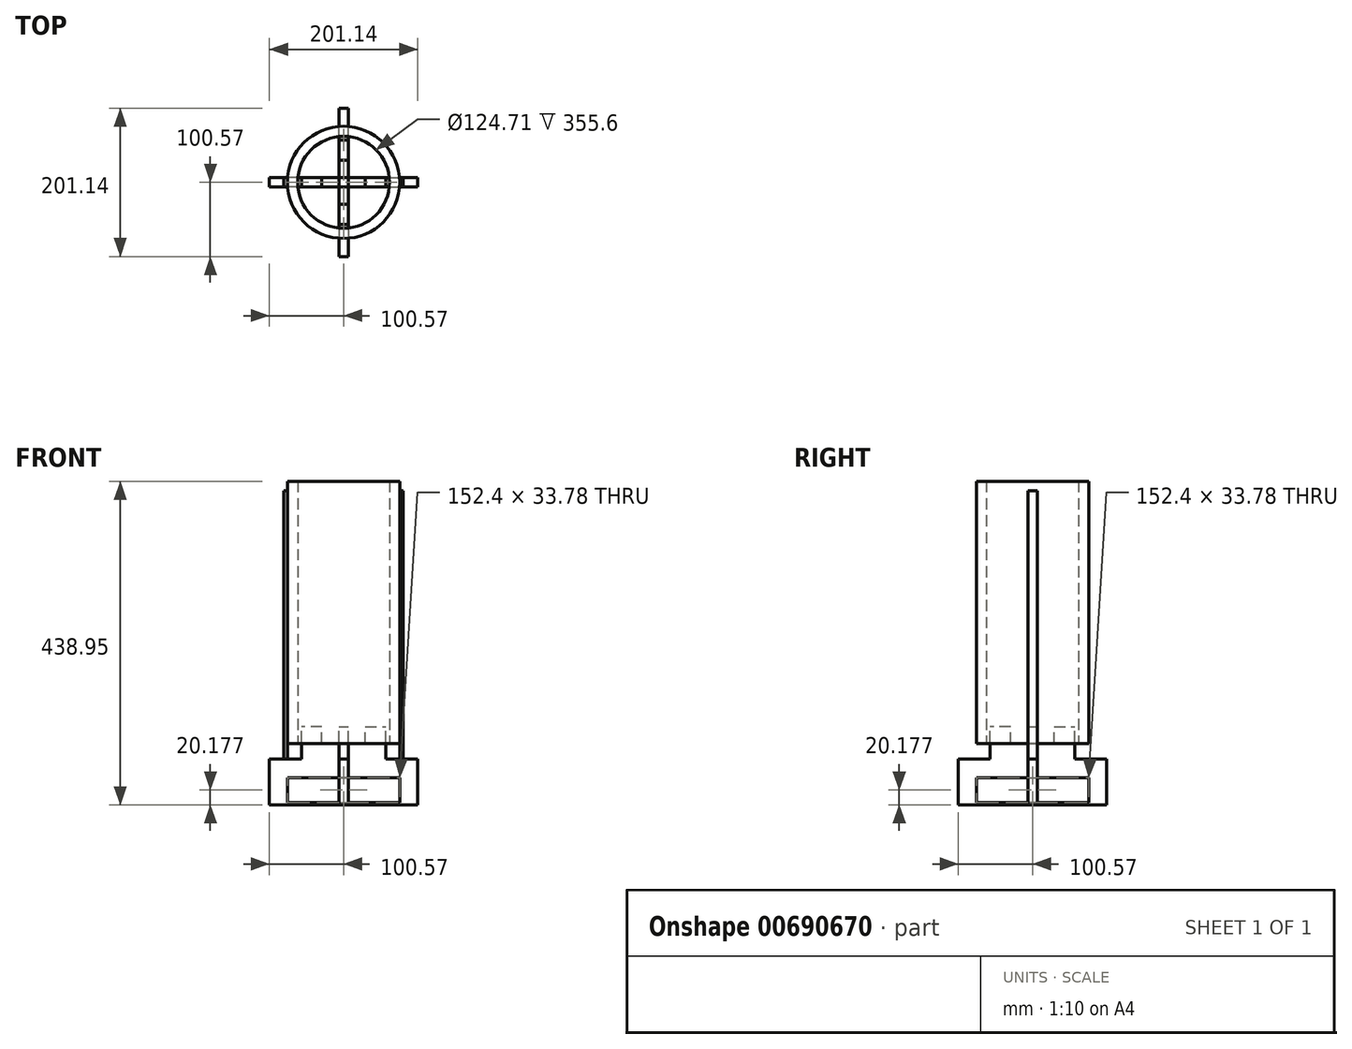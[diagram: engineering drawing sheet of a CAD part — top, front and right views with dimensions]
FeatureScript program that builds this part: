
annotation { "Feature Type Name" : "Feature", "Feature Type Description" : "" }
export const myFeature = defineFeature(function(context is Context, id is Id, definition is map)
    precondition{}
    {
        {
            var Q0;
            Q0=qCreatedBy(makeId("Top.planeOp"),FACE);
            var sketch = newSketch(context, id + "F0", { "sketchPlane" : qUnion([Q0])});
            skCircle(sketch, "E0", {"center": v(0, 0) * mm, "radius": 76.2 * mm});
            skCircle(sketch, "E1.0", {"center": v(0, 0) * mm, "radius": 62.36 * mm});
            skSolve(sketch);
        }
        {
            var Q0;
            Q0=qSketchRegion(id+"F0",true);
            extrude(context, id + "F1", {"entities" : qUnion([Q0]), "depth" : 355.6 * mm, "offsetDistance" : 25.4 * mm});
        }
        {
            var Q0;
            Q0=qCreatedBy(makeId("Front.planeOp"),FACE);
            var sketch = newSketch(context, id + "F2", { "sketchPlane" : qUnion([Q0])});
            skLineSegment(sketch, "E2", {"start": v(0, -20.88) * mm, "end": v(76.2, -20.88) * mm});
            skLineSegment(sketch, "E3", {"start": v(76.2, -46.28) * mm, "end": v(76.2, -25.4) * mm});
            skLineSegment(sketch, "E4", {"start": v(76.2, -46.28) * mm, "end": v(0, -46.28) * mm});
            skLineSegment(sketch, "E5", {"start": v(76.2, -20.88) * mm, "end": v(76.2, -46.28) * mm});
            skLineSegment(sketch, "E6", {"start": v(76.2, -46.28) * mm, "end": v(76.2, -46.28) * mm});
            skLineSegment(sketch, "E7", {"start": v(76.2, -25.4) * mm, "end": v(76.2, -46.28) * mm});
            skLineSegment(sketch, "E8", {"start": v(0, -20.88) * mm, "end": v(0, -46.28) * mm});
            skLineSegment(sketch, "E9.top", {"start": v(76.2, -83.35) * mm, "end": v(76.2, -83.35) * mm});
            skLineSegment(sketch, "E9.right", {"start": v(76.2, -25.4) * mm, "end": v(76.2, -83.35) * mm});
            skLineSegment(sketch, "E10.MirrorCS", {"start": v(-76.2, -46.28) * mm, "end": v(-76.2, -46.28) * mm});
            skLineSegment(sketch, "E11.MirrorCS", {"start": v(-76.2, -20.88) * mm, "end": v(-76.2, -46.28) * mm});
            skLineSegment(sketch, "E12.MirrorCS", {"start": v(-76.2, -25.4) * mm, "end": v(-76.2, -25.4) * mm});
            skLineSegment(sketch, "E13.MirrorCS", {"start": v(-76.2, -25.4) * mm, "end": v(-76.2, -83.35) * mm});
            skLineSegment(sketch, "E14.MirrorCS", {"start": v(-76.2, -46.28) * mm, "end": v(0, -46.28) * mm});
            skLineSegment(sketch, "E15.MirrorCS", {"start": v(-76.2, -46.28) * mm, "end": v(-76.2, -25.4) * mm});
            skLineSegment(sketch, "E16.MirrorCS", {"start": v(0, -20.88) * mm, "end": v(-76.2, -20.88) * mm});
            skLineSegment(sketch, "E17.MirrorCS", {"start": v(-76.2, -25.4) * mm, "end": v(-76.2, -46.28) * mm});
            skLineSegment(sketch, "E18.MirrorCS", {"start": v(-76.2, -83.35) * mm, "end": v(-76.2, -83.35) * mm});
            skLineSegment(sketch, "E19.bottom", {"start": v(-76.2, -83.35) * mm, "end": v(76.2, -83.35) * mm});
            skLineSegment(sketch, "E19.top", {"start": v(-76.2, -80.06) * mm, "end": v(76.2, -80.06) * mm});
            skLineSegment(sketch, "E19.left", {"start": v(-76.2, -83.35) * mm, "end": v(-76.2, -80.06) * mm});
            skLineSegment(sketch, "E19.right", {"start": v(76.2, -83.35) * mm, "end": v(76.2, -80.06) * mm});
            skLineSegment(sketch, "E20.bottom", {"start": v(76.2, -20.88) * mm, "end": v(100.57, -20.88) * mm});
            skLineSegment(sketch, "E20.top", {"start": v(76.2, -83.35) * mm, "end": v(100.57, -83.35) * mm});
            skLineSegment(sketch, "E20.left", {"start": v(76.2, -20.88) * mm, "end": v(76.2, -83.35) * mm});
            skLineSegment(sketch, "E20.right", {"start": v(100.57, -20.88) * mm, "end": v(100.57, -83.35) * mm});
            skLineSegment(sketch, "E21.MirrorCS", {"start": v(-100.57, -20.88) * mm, "end": v(-100.57, -83.35) * mm});
            skLineSegment(sketch, "E22.MirrorCS", {"start": v(-76.2, -20.88) * mm, "end": v(-100.57, -20.88) * mm});
            skLineSegment(sketch, "E23.MirrorCS", {"start": v(-76.2, -83.35) * mm, "end": v(-100.57, -83.35) * mm});
            skLineSegment(sketch, "E24.0", {"start": v(-62.36, 0) * mm, "end": v(62.36, 0) * mm});
            skLineSegment(sketch, "E25.bottom", {"start": v(0, -20.88) * mm, "end": v(57.23, -20.88) * mm});
            skLineSegment(sketch, "E25.top", {"start": v(0, 0) * mm, "end": v(57.23, 0) * mm});
            skLineSegment(sketch, "E25.left", {"start": v(0, -20.88) * mm, "end": v(0, 0) * mm});
            skLineSegment(sketch, "E25.right", {"start": v(57.23, -20.88) * mm, "end": v(57.23, 0) * mm});
            skLineSegment(sketch, "E26.bottom", {"start": v(29.62, 0) * mm, "end": v(57.23, 0) * mm});
            skLineSegment(sketch, "E26.top", {"start": v(29.62, 22.92) * mm, "end": v(57.23, 22.92) * mm});
            skLineSegment(sketch, "E26.left", {"start": v(29.62, 0) * mm, "end": v(29.62, 22.92) * mm});
            skLineSegment(sketch, "E26.right", {"start": v(57.23, 0) * mm, "end": v(57.23, 22.92) * mm});
            skLineSegment(sketch, "E27.MirrorCS", {"start": v(-29.62, 0) * mm, "end": v(-29.62, 22.92) * mm});
            skLineSegment(sketch, "E28.MirrorCS", {"start": v(-29.62, 22.92) * mm, "end": v(-57.23, 22.92) * mm});
            skLineSegment(sketch, "E29.MirrorCS", {"start": v(-57.23, 0) * mm, "end": v(-57.23, 22.92) * mm});
            skLineSegment(sketch, "E30.MirrorCS", {"start": v(-57.23, -20.88) * mm, "end": v(-57.23, 0) * mm});
            skSolve(sketch);
        }
        {
            var Q0;
            Q0=qSketchRegion(id+"F2",true);
            extrude(context, id + "F3", {"entities" : qUnion([Q0]), "endBound" : BoundingType.SYMMETRIC, "depth" : 12.7 * mm, "offsetDistance" : 25.4 * mm});
        }
        {
            var Q0;
            Q0=makeQuery(id+"F3.opExtrude","SWEPT_BODY",BODY,{"disambiguationData":[OSD([sQuery(id+"F2.wireOp",EDGE,"E2"),sQuery(id+"F2.wireOp",EDGE,"E3"),sQuery(id+"F2.wireOp",EDGE,"E4"),sQuery(id+"F2.wireOp",EDGE,"E5"),sQuery(id+"F2.wireOp",EDGE,"E6"),sQuery(id+"F2.wireOp",EDGE,"E7"),sQuery(id+"F2.wireOp",EDGE,"yYa1QQtk-rfeQ-uA0k-yN95-LENgFDuBBmhA"),sQuery(id+"F2.wireOp",EDGE,"RaL1Y38n-DL0R-HpUy-0Yu0-hKOuieMtGCDP"),sQuery(id+"F2.wireOp",EDGE,"KzeCX9vK-PA9l-fBDc-L8z4-hnWVkcK37siH"),sQuery(id+"F2.wireOp",EDGE,"7a3115bd-42c9-43fa-886f-b7d7f014f3800.MirrorCS"),sQuery(id+"F2.wireOp",EDGE,"93714e8b-1b55-43fa-9f0a-1818bfe9d4330.MirrorCS"),sQuery(id+"F2.wireOp",EDGE,"f685ec73-5cd7-40c9-a0cc-09a82770efb00.MirrorCS"),sQuery(id+"F2.wireOp",EDGE,"605de593-ab4b-4a38-8b95-8d2e6ad95e7e0.MirrorCS"),sQuery(id+"F2.wireOp",EDGE,"bd68596d-ea5b-43b6-8ec0-eaa4091035650.MirrorCS"),sQuery(id+"F2.wireOp",EDGE,"6dadb6d6-938b-41b2-89eb-21b29489f2620.MirrorCS"),sQuery(id+"F2.wireOp",EDGE,"35a6b2d6-89f1-42be-bee9-e52b24f0a85c0.MirrorCS"),sQuery(id+"F2.wireOp",EDGE,"99d46e2b-beb4-45a8-a67b-b38dd53197940.MirrorCS"),sQuery(id+"F2.wireOp",EDGE,"687b68df-4fec-4741-9a90-ace4315f9af80.MirrorCS")])]});
            transform(context, id + "F4", {"entities" : qUnion([Q0]), "transformType" : TransformType.COPY});
        }
        {
            var Q0;
            Q0=makeQuery(id+"F3.opExtrude","SWEPT_BODY",BODY,{"disambiguationData":[OSD([sQuery(id+"F2.wireOp",EDGE,"E2"),sQuery(id+"F2.wireOp",EDGE,"E3"),sQuery(id+"F2.wireOp",EDGE,"E4"),sQuery(id+"F2.wireOp",EDGE,"E5"),sQuery(id+"F2.wireOp",EDGE,"E6"),sQuery(id+"F2.wireOp",EDGE,"E7"),sQuery(id+"F2.wireOp",EDGE,"yYa1QQtk-rfeQ-uA0k-yN95-LENgFDuBBmhA"),sQuery(id+"F2.wireOp",EDGE,"RaL1Y38n-DL0R-HpUy-0Yu0-hKOuieMtGCDP"),sQuery(id+"F2.wireOp",EDGE,"KzeCX9vK-PA9l-fBDc-L8z4-hnWVkcK37siH"),sQuery(id+"F2.wireOp",EDGE,"7a3115bd-42c9-43fa-886f-b7d7f014f3800.MirrorCS"),sQuery(id+"F2.wireOp",EDGE,"93714e8b-1b55-43fa-9f0a-1818bfe9d4330.MirrorCS"),sQuery(id+"F2.wireOp",EDGE,"f685ec73-5cd7-40c9-a0cc-09a82770efb00.MirrorCS"),sQuery(id+"F2.wireOp",EDGE,"605de593-ab4b-4a38-8b95-8d2e6ad95e7e0.MirrorCS"),sQuery(id+"F2.wireOp",EDGE,"bd68596d-ea5b-43b6-8ec0-eaa4091035650.MirrorCS"),sQuery(id+"F2.wireOp",EDGE,"6dadb6d6-938b-41b2-89eb-21b29489f2620.MirrorCS"),sQuery(id+"F2.wireOp",EDGE,"35a6b2d6-89f1-42be-bee9-e52b24f0a85c0.MirrorCS"),sQuery(id+"F2.wireOp",EDGE,"99d46e2b-beb4-45a8-a67b-b38dd53197940.MirrorCS"),sQuery(id+"F2.wireOp",EDGE,"687b68df-4fec-4741-9a90-ace4315f9af80.MirrorCS")])]});
            var Q1;
            Q1=sQuery(id+"F2.wireOp",EDGE,"E8");
            transform(context, id + "F5", {"entities" : qUnion([Q0]), "transformType" : TransformType.ROTATION, "transformAxis" : qUnion([Q1]), "angle" : 90 * degree, "makeCopy" : false});
        }
        {
            var Q0;
            Q0=makeQuery(id+"F4.opPattern","COPY",FACE,{"derivedFrom":makeQuery(id+"F3.opExtrude","CAP_FACE",FACE,{"disambiguationData":[OSD([sQuery(id+"F2.wireOp",EDGE,"E2"),sQuery(id+"F2.wireOp",EDGE,"E3"),sQuery(id+"F2.wireOp",EDGE,"E4"),sQuery(id+"F2.wireOp",EDGE,"E5"),sQuery(id+"F2.wireOp",EDGE,"E6"),sQuery(id+"F2.wireOp",EDGE,"E7"),sQuery(id+"F2.wireOp",EDGE,"E9.bottom"),sQuery(id+"F2.wireOp",EDGE,"E9.top"),sQuery(id+"F2.wireOp",EDGE,"E9.right"),sQuery(id+"F2.wireOp",EDGE,"6d3937cc-c99b-4de3-b3db-85ad403e89ce3.MirrorCS"),sQuery(id+"F2.wireOp",EDGE,"E13.MirrorCS"),sQuery(id+"F2.wireOp",EDGE,"6d3937cc-c99b-4de3-b3db-85ad403e89ce8.MirrorCS"),sQuery(id+"F2.wireOp",EDGE,"E14.MirrorCS"),sQuery(id+"F2.wireOp",EDGE,"E12.MirrorCS"),sQuery(id+"F2.wireOp",EDGE,"6d3937cc-c99b-4de3-b3db-85ad403e89ce11.MirrorCS"),sQuery(id+"F2.wireOp",EDGE,"E15.MirrorCS"),sQuery(id+"F2.wireOp",EDGE,"E16.MirrorCS"),sQuery(id+"F2.wireOp",EDGE,"6d3937cc-c99b-4de3-b3db-85ad403e89ce15.MirrorCS"),sQuery(id+"F2.wireOp",EDGE,"E17.MirrorCS")])],"isStart":false}),"instanceName":"1"});
            var sketch = newSketch(context, id + "F6", { "sketchPlane" : qUnion([Q0])});
            skLineSegment(sketch, "E31.bottom", {"start": v(76.2, -20.88) * mm, "end": v(80.84, -20.88) * mm});
            skLineSegment(sketch, "E31.top", {"start": v(76.2, 342.69) * mm, "end": v(80.84, 342.69) * mm});
            skLineSegment(sketch, "E31.left", {"start": v(76.2, -20.88) * mm, "end": v(76.2, 342.69) * mm});
            skLineSegment(sketch, "E31.right", {"start": v(80.84, -20.88) * mm, "end": v(80.84, 342.69) * mm});
            skLineSegment(sketch, "E32.0", {"start": v(76.2, -20.88) * mm, "end": v(100.57, -20.88) * mm});
            skLineSegment(sketch, "E33.0.0", {"start": v(100.57, -20.88) * mm, "end": v(57.23, -20.88) * mm});
            skLineSegment(sketch, "E33.0.2", {"start": v(57.23, -20.88) * mm, "end": v(100.57, -20.88) * mm});
            skSolve(sketch);
        }
        {
            var Q0;
            Q0=makeQuery(id+"F6.imprint","IMPRINT",FACE,{"disambiguationData":[TD([[makeQuery(id+"F6.imprint","IMPRINT",EDGE,{"derivedFrom":sQuery(id+"F6.wireOp",EDGE,"E31.top")}),-1.0]])]});
            extrude(context, id + "F7", {"entities" : qUnion([Q0]), "oppositeDirection" : true, "depth" : 12.7 * mm, "offsetDistance" : 25.4 * mm});
        }
        {
            var Q0;
            Q0=makeQuery(id+"F7.opExtrude","SWEPT_BODY",BODY,{"disambiguationData":[OSD([sQuery(id+"F6.wireOp",EDGE,"E31.bottom"),sQuery(id+"F6.wireOp",EDGE,"E31.top"),sQuery(id+"F6.wireOp",EDGE,"E31.left"),sQuery(id+"F6.wireOp",EDGE,"E31.right")])]});
            var Q1;
            Q1=sQuery(id+"F2.wireOp",EDGE,"E8");
            circularPattern(context, id + "F8", {"entities" : qUnion([Q0]), "axis" : qUnion([Q1]), "angle" : 360 * degree, "instanceCount" : 2, "equalSpace" : true});
        }
    });
